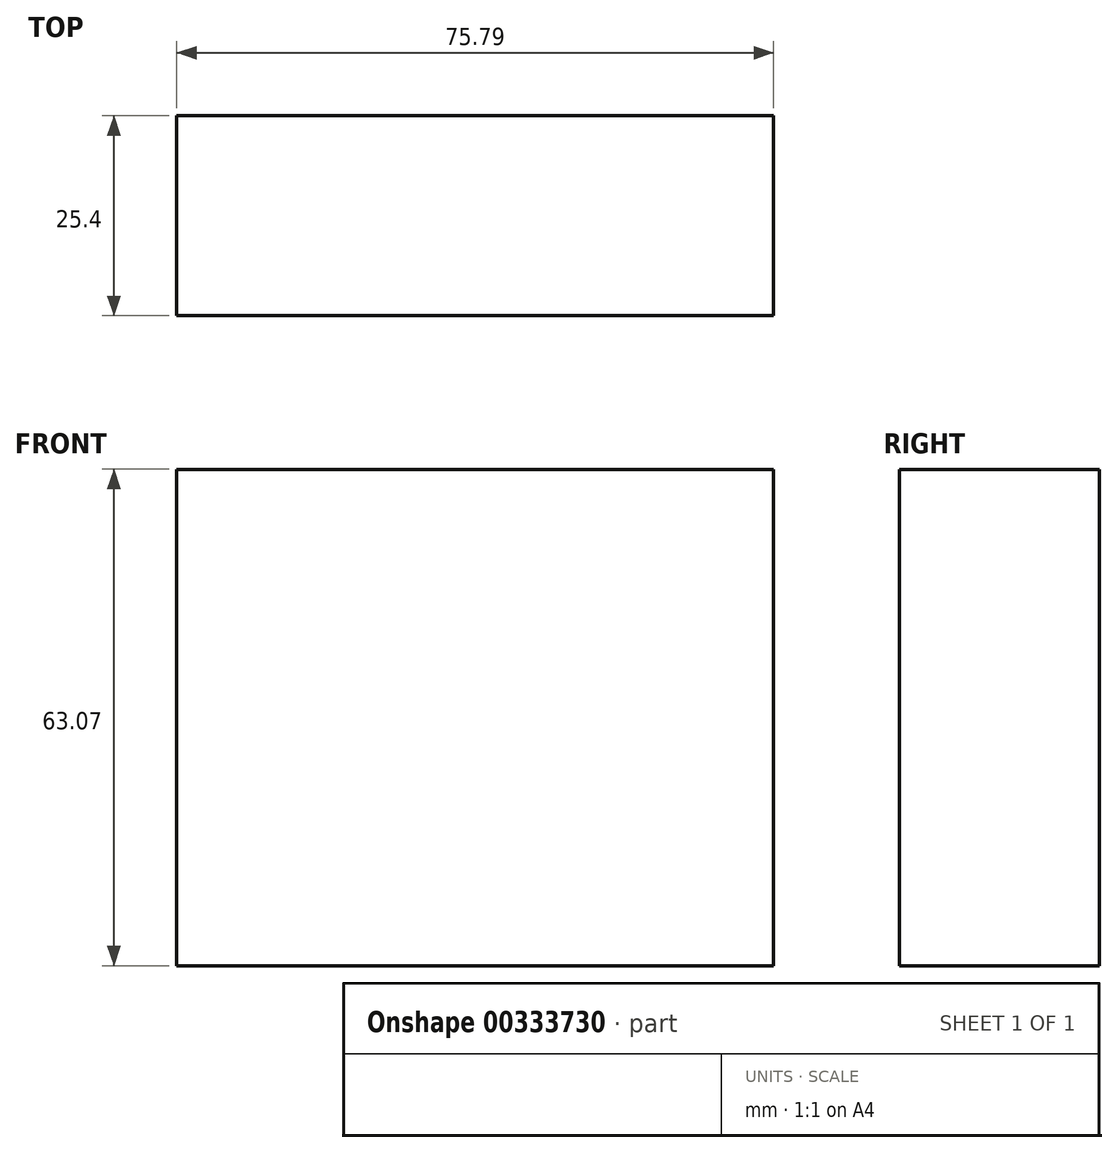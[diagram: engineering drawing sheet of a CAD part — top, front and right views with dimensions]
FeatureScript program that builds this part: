
annotation { "Feature Type Name" : "Feature", "Feature Type Description" : "" }
export const myFeature = defineFeature(function(context is Context, id is Id, definition is map)
    precondition{}
    {
        {
            var Q0;
            Q0=qCreatedBy(makeId("Front.planeOp"),FACE);
            var sketch = newSketch(context, id + "F0", { "sketchPlane" : qUnion([Q0])});
            skLineSegment(sketch, "E0", {"start": v(0, 63.07) * mm, "end": v(75.79, 63.07) * mm});
            skLineSegment(sketch, "E1", {"start": v(75.79, 63.07) * mm, "end": v(75.79, 0) * mm});
            skLineSegment(sketch, "E2", {"start": v(75.79, 0) * mm, "end": v(0, 0) * mm});
            skLineSegment(sketch, "E3", {"start": v(0, 0) * mm, "end": v(0, 63.07) * mm});
            skSolve(sketch);
        }
        {
            var Q0;
            Q0 = qSketchRegion(id + "F0", true);
            extrude(context, id + "F1", {"entities" : qUnion([Q0]), "depth" : 25.4 * mm});
        }
    });
